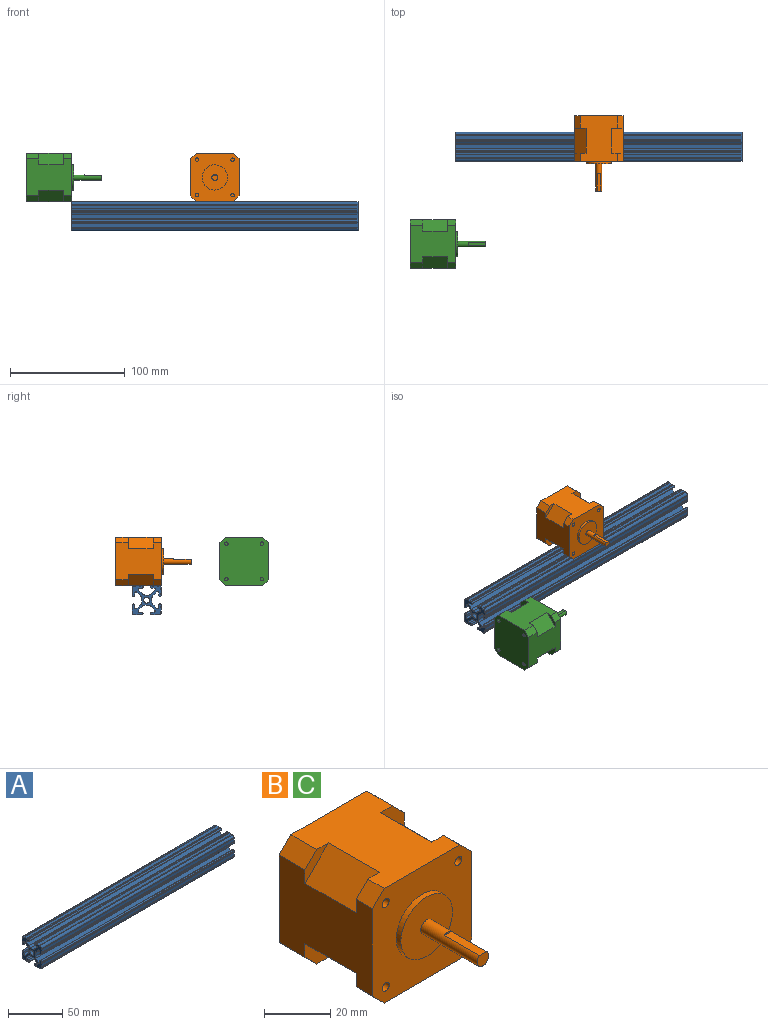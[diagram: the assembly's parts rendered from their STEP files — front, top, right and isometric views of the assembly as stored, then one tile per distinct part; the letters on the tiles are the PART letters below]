
ASSEMBLY  parts=3 mates=4
PART A: 99 faces, bbox 250x25.4x25.4 mm
  f0: cylinder r=2.6mm len=250mm, axis (-1,0,0), area 4089.6mm2, adj f1,f2
  f1: plane 25.4x25.4mm, normal (1,0,0), area 280.1mm2, adj f0,f3,f4,f5,f6,f7,f8,f9
  f2: plane 25.4x25.4mm, normal (-1,0,0), area 280.1mm2, adj f0,f3,f4,f5,f6,f7,f8,f9
  f3: plane 250x3.23mm, normal (0,0.71,0.71), area 1140mm2, adj f1,f2,f4,f98
  f4: cylinder r=1.08mm len=250mm, axis (-1,0,0), area 636.7mm2, adj f1,f2,f3,f5
  f5: plane 250x2.13mm, normal (0,-1,0), area 532.2mm2, adj f1,f2,f4,f6
  f6: cylinder r=1.06mm len=250mm, axis (-1,0,0), area 410.9mm2, adj f1,f2,f5,f7
  f7: plane 250x0.11mm, normal (0,0,1), area 27.9mm2, adj f1,f2,f6,f8
  f8: cylinder r=1.06mm len=250mm, axis (-1,0,0), area 410.9mm2, adj f1,f2,f7,f9
  f9: plane 250x1.03mm, normal (0,1,0), area 257.4mm2, adj f1,f2,f8,f10
  f10: cylinder r=0.51mm len=250mm, axis (-1,0,0), area 399mm2, adj f1,f2,f9,f11
  f11: plane 250x3.22mm, normal (0,1,0), area 804.3mm2, adj f1,f2,f10,f12
  f12: cylinder r=0.51mm len=250mm, axis (-1,0,0), area 398.9mm2, adj f1,f2,f11,f13
  f13: cylinder r=2.11mm len=250mm, axis (-1,0,0), area 840.6mm2, adj f1,f2,f12,f14
  f14: cylinder r=0.51mm len=250mm, axis (-1,0,0), area 398.9mm2, adj f1,f2,f13,f15
  f15: plane 250x3.22mm, normal (0,0,-1), area 804.4mm2, adj f1,f2,f14,f16
  f16: cylinder r=0.51mm len=250mm, axis (-1,0,0), area 399mm2, adj f1,f2,f15,f17
  f17: plane 250x1.03mm, normal (0,0,-1), area 257.4mm2, adj f1,f2,f16,f18
  f18: cylinder r=1.06mm len=250mm, axis (-1,0,0), area 410.9mm2, adj f1,f2,f17,f19
  f19: plane 250x0.11mm, normal (0,-1,0), area 27.9mm2, adj f1,f2,f18,f20
  f20: cylinder r=1.06mm len=250mm, axis (-1,0,0), area 410.9mm2, adj f1,f2,f19,f21
  f21: plane 250x2.11mm, normal (0,0,1), area 528.6mm2, adj f1,f2,f20,f22
  f22: cylinder r=1.03mm len=250mm, axis (-1,0,0), area 604.9mm2, adj f1,f2,f21,f23
  f23: plane 250x3.3mm, normal (0,-0.71,-0.71), area 1164mm2, adj f1,f2,f22,f24
  f24: cylinder r=3.19mm len=250mm, axis (-1,0,0), area 624.1mm2, adj f1,f2,f23,f25
  f25: plane 250x3.19mm, normal (0,0,-1), area 796.6mm2, adj f1,f2,f24,f26
  f26: cylinder r=3.2mm len=250mm, axis (-1,0,0), area 624.1mm2, adj f1,f2,f25,f27
  f27: plane 250x3.3mm, normal (0,0.71,-0.71), area 1164mm2, adj f1,f2,f26,f28
  f28: cylinder r=1.03mm len=250mm, axis (-1,0,0), area 604.9mm2, adj f1,f2,f27,f29
  f29: plane 250x2.11mm, normal (0,0,1), area 528.6mm2, adj f1,f2,f28,f30
  f30: cylinder r=1.06mm len=250mm, axis (-1,0,0), area 410.9mm2, adj f1,f2,f29,f31
  f31: plane 250x0.11mm, normal (0,1,0), area 27.9mm2, adj f1,f2,f30,f32
  f32: cylinder r=1.06mm len=250mm, axis (-1,0,0), area 410.9mm2, adj f1,f2,f31,f33
  f33: plane 250x1.03mm, normal (0,0,-1), area 257.4mm2, adj f1,f2,f32,f34
  f34: cylinder r=0.51mm len=250mm, axis (-1,0,0), area 399mm2, adj f1,f2,f33,f35
  f35: plane 250x3.22mm, normal (0,0,-1), area 804.3mm2, adj f1,f2,f34,f36
  f36: cylinder r=0.51mm len=250mm, axis (-1,0,0), area 398.9mm2, adj f1,f2,f35,f37
  f37: cylinder r=2.11mm len=250mm, axis (-1,0,0), area 840.6mm2, adj f1,f2,f36,f38
  f38: cylinder r=0.51mm len=250mm, axis (-1,0,0), area 399mm2, adj f1,f2,f37,f39
  f39: plane 250x3.22mm, normal (0,-1,0), area 804.3mm2, adj f1,f2,f38,f40
  f40: cylinder r=0.51mm len=250mm, axis (-1,0,0), area 399mm2, adj f1,f2,f39,f41
  f41: plane 250x1.03mm, normal (0,-1,0), area 257.4mm2, adj f1,f2,f40,f42
  f42: cylinder r=1.06mm len=250mm, axis (-1,0,0), area 410.9mm2, adj f1,f2,f41,f43
  f43: plane 250x0.11mm, normal (0,0,1), area 27.9mm2, adj f1,f2,f42,f44
  f44: cylinder r=1.06mm len=250mm, axis (-1,0,0), area 410.9mm2, adj f1,f2,f43,f45
  f45: plane 250x2.19mm, normal (0,1,0), area 547.3mm2, adj f1,f2,f44,f46
  f46: cylinder r=1.03mm len=250mm, axis (-1,0,0), area 609.4mm2, adj f1,f2,f45,f47
  f47: plane 250x3.31mm, normal (0,-0.71,0.71), area 1168.5mm2, adj f1,f2,f46,f48
  f48: cylinder r=3.2mm len=250mm, axis (-1,0,0), area 622.2mm2, adj f1,f2,f47,f49
  f49: plane 250x3.31mm, normal (0,-1,0), area 827.9mm2, adj f1,f2,f48,f50
  f50: cylinder r=3.2mm len=250mm, axis (-1,0,0), area 622.3mm2, adj f1,f2,f49,f51
  f51: plane 250x3.31mm, normal (0,-0.71,-0.71), area 1168.5mm2, adj f1,f2,f50,f52
  f52: cylinder r=1.03mm len=250mm, axis (-1,0,0), area 609.4mm2, adj f1,f2,f51,f53
  f53: plane 250x2.19mm, normal (0,1,0), area 547.3mm2, adj f1,f2,f52,f54
  f54: cylinder r=1.06mm len=250mm, axis (-1,0,0), area 410.9mm2, adj f1,f2,f53,f55
  f55: plane 250x0.11mm, normal (0,0,-1), area 27.9mm2, adj f1,f2,f54,f56
  f56: cylinder r=1.06mm len=250mm, axis (-1,0,0), area 410.9mm2, adj f1,f2,f55,f57
  f57: plane 250x1.03mm, normal (0,-1,0), area 257.4mm2, adj f1,f2,f56,f58
  f58: cylinder r=0.51mm len=250mm, axis (-1,0,0), area 399mm2, adj f1,f2,f57,f59
  f59: plane 250x3.22mm, normal (0,-1,0), area 804.3mm2, adj f1,f2,f58,f60
  f60: cylinder r=0.51mm len=250mm, axis (-1,0,0), area 399mm2, adj f1,f2,f59,f61
  f61: cylinder r=2.11mm len=250mm, axis (-1,0,0), area 840.6mm2, adj f1,f2,f60,f62
  f62: cylinder r=0.51mm len=250mm, axis (-1,0,0), area 398.9mm2, adj f1,f2,f61,f63
  f63: plane 250x3.22mm, normal (0,0,1), area 804.3mm2, adj f1,f2,f62,f64
  f64: cylinder r=0.51mm len=250mm, axis (-1,0,0), area 399mm2, adj f1,f2,f63,f65
  f65: plane 250x1.03mm, normal (0,0,1), area 257.4mm2, adj f1,f2,f64,f66
  f66: cylinder r=1.06mm len=250mm, axis (-1,0,0), area 410.9mm2, adj f1,f2,f65,f67
  f67: plane 250x0.11mm, normal (0,1,0), area 27.9mm2, adj f1,f2,f66,f68
  f68: cylinder r=1.06mm len=250mm, axis (-1,0,0), area 410.9mm2, adj f1,f2,f67,f69
  f69: plane 250x2.11mm, normal (0,0,-1), area 528.6mm2, adj f1,f2,f68,f70
  f70: cylinder r=1.03mm len=250mm, axis (-1,0,0), area 604.9mm2, adj f1,f2,f69,f71
  f71: plane 250x3.3mm, normal (0,0.71,0.71), area 1164.1mm2, adj f1,f2,f70,f72
  f72: cylinder r=3.19mm len=250mm, axis (-1,0,0), area 624mm2, adj f1,f2,f71,f73
  f73: plane 250x3.19mm, normal (0,0,1), area 796.6mm2, adj f1,f2,f72,f74
  f74: cylinder r=3.19mm len=250mm, axis (-1,0,0), area 624.1mm2, adj f1,f2,f73,f75
  f75: plane 250x3.3mm, normal (0,-0.71,0.71), area 1164mm2, adj f1,f2,f74,f76
  f76: cylinder r=1.03mm len=250mm, axis (-1,0,0), area 604.9mm2, adj f1,f2,f75,f77
  f77: plane 250x2.11mm, normal (0,0,-1), area 528.6mm2, adj f1,f2,f76,f78
  f78: cylinder r=1.06mm len=250mm, axis (-1,0,0), area 410.9mm2, adj f1,f2,f77,f79
  f79: plane 250x0.11mm, normal (0,-1,0), area 27.9mm2, adj f1,f2,f78,f80
  f80: cylinder r=1.06mm len=250mm, axis (-1,0,0), area 410.9mm2, adj f1,f2,f79,f81
  f81: plane 250x1.03mm, normal (0,0,1), area 257.4mm2, adj f1,f2,f80,f82
  f82: cylinder r=0.51mm len=250mm, axis (-1,0,0), area 399mm2, adj f1,f2,f81,f83
  f83: plane 250x3.22mm, normal (0,0,1), area 804.4mm2, adj f1,f2,f82,f84
  f84: cylinder r=0.51mm len=250mm, axis (-1,0,0), area 398.9mm2, adj f1,f2,f83,f85
  f85: cylinder r=2.11mm len=250mm, axis (-1,0,0), area 840.6mm2, adj f1,f2,f84,f86
  f86: cylinder r=0.51mm len=250mm, axis (-1,0,0), area 398.9mm2, adj f1,f2,f85,f87
  f87: plane 250x3.22mm, normal (0,1,0), area 804.3mm2, adj f1,f2,f86,f88
  f88: cylinder r=0.51mm len=250mm, axis (-1,0,0), area 399mm2, adj f1,f2,f87,f89
  f89: plane 250x1.03mm, normal (0,1,0), area 257.4mm2, adj f1,f2,f88,f90
  f90: cylinder r=1.06mm len=250mm, axis (-1,0,0), area 410.9mm2, adj f1,f2,f89,f91
  f91: plane 250x0.11mm, normal (0,0,-1), area 27.9mm2, adj f1,f2,f90,f92
  f92: cylinder r=1.06mm len=250mm, axis (-1,0,0), area 410.9mm2, adj f1,f2,f91,f93
  f93: plane 250x2.13mm, normal (0,-1,0), area 532.3mm2, adj f1,f2,f92,f94
  f94: cylinder r=1.08mm len=250mm, axis (-1,0,0), area 636.6mm2, adj f1,f2,f93,f95
  f95: plane 250x3.23mm, normal (0,0.71,-0.71), area 1140mm2, adj f1,f2,f94,f96
  f96: cylinder r=3.19mm len=250mm, axis (-1,0,0), area 622.5mm2, adj f1,f2,f95,f97
  f97: plane 250x3.42mm, normal (0,1,0), area 854.6mm2, adj f1,f2,f96,f98
  f98: cylinder r=3.19mm len=250mm, axis (-1,0,0), area 622.5mm2, adj f1,f2,f3,f97
PART B: 48 faces, bbox 42.3x65.8x42.3 mm
  f0: plane 10x10mm, normal (0,1,0), area 37.5mm2, adj f4,f5,f9,f27
  f1: plane 10x10mm, normal (0,1,0), area 37.5mm2, adj f5,f6,f10,f30
  f2: plane 10x10mm, normal (0,1,0), area 37.5mm2, adj f6,f7,f11,f29
  f3: plane 42.3x42.3mm, normal (0,-1,0), area 1330.9mm2, adj f4,f5,f6,f7,f9,f10,f11,f12
  f4: plane 39.8x32.3mm, normal (-1,0,0), area 1067.5mm2, adj f0,f3,f8,f9,f12,f27,f28,f31
  f5: plane 39.8x32.3mm, normal (0,0,-1), area 1067.5mm2, adj f0,f1,f3,f9,f10,f27,f30,f31
  f6: plane 39.8x32.3mm, normal (1,0,0), area 1067.5mm2, adj f1,f2,f3,f10,f11,f29,f30,f33
  f7: plane 39.8x32.3mm, normal (0,0,1), area 1067.5mm2, adj f2,f3,f8,f11,f12,f28,f29,f32
  f8: plane 10x10mm, normal (0,1,0), area 37.5mm2, adj f4,f7,f12,f28
  f9: plane 7x5mm, normal (-0.71,0,-0.71), area 49.5mm2, adj f0,f3,f4,f5
  f10: plane 7x5mm, normal (0.71,0,-0.71), area 49.5mm2, adj f1,f3,f5,f6
  f11: plane 7x5mm, normal (0.71,0,0.71), area 49.5mm2, adj f2,f3,f6,f7
  f12: plane 7x5mm, normal (-0.71,0,0.71), area 49.5mm2, adj f3,f4,f7,f8
  f13: cylinder r=11mm len=22mm, axis (0,1,0), area 138.2mm2, adj f3,f14
  f14: plane 22x22mm, normal (0,-1,0), area 360.5mm2, adj f13,f23
  f15: cylinder r=1.5mm len=4.5mm, axis (0,-1,0), area 42.4mm2, adj f3,f16
  f16: plane 3x3mm, normal (0,-1,0), area 7.1mm2, adj f15
  f17: cylinder r=1.5mm len=4.5mm, axis (0,-1,0), area 42.4mm2, adj f3,f18
  f18: plane 3x3mm, normal (0,-1,0), area 7.1mm2, adj f17
  f19: cylinder r=1.5mm len=4.5mm, axis (0,-1,0), area 42.4mm2, adj f3,f20
  f20: plane 3x3mm, normal (0,-1,0), area 7.1mm2, adj f19
  f21: cylinder r=1.5mm len=4.5mm, axis (0,-1,0), area 42.4mm2, adj f3,f22
  f22: plane 3x3mm, normal (0,-1,0), area 7.1mm2, adj f21
  f23: cylinder r=2.5mm len=24mm, axis (0,1,0), area 328.7mm2, adj f14,f24,f25,f26
  f24: plane 5x4.5mm, normal (0,-1,0), area 18.6mm2, adj f23,f25
  f25: plane 15x3mm, normal (0,0,1), area 45mm2, adj f23,f24,f26
  f26: plane 3x0.5mm, normal (0,-1,0), area 1mm2, adj f23,f25
  f27: plane 21.8x10mm, normal (-0.71,0,-0.71), area 308.3mm2, adj f0,f4,f5,f31
  f28: plane 21.8x10mm, normal (-0.71,0,0.71), area 308.3mm2, adj f4,f7,f8,f32
  f29: plane 21.8x10mm, normal (0.71,0,0.71), area 308.3mm2, adj f2,f6,f7,f33
  f30: plane 21.8x10mm, normal (0.71,0,-0.71), area 308.3mm2, adj f1,f5,f6,f34
  f31: plane 10x10mm, normal (0,-1,0), area 37.5mm2, adj f4,f5,f27,f37
  f32: plane 10x10mm, normal (0,-1,0), area 37.5mm2, adj f4,f7,f28,f36
  f33: plane 10x10mm, normal (0,-1,0), area 37.5mm2, adj f6,f7,f29,f39
  f34: plane 10x10mm, normal (0,-1,0), area 37.5mm2, adj f5,f6,f30,f38
  f35: plane 42.3x42.3mm, normal (0,1,0), area 1711mm2, adj f4,f5,f6,f7,f36,f37,f38,f39
  f36: plane 11x5mm, normal (-0.71,0,0.71), area 77.8mm2, adj f4,f7,f32,f35
  f37: plane 11x5mm, normal (-0.71,0,-0.71), area 77.8mm2, adj f4,f5,f31,f35
  f38: plane 11x5mm, normal (0.71,0,-0.71), area 77.8mm2, adj f5,f6,f34,f35
  f39: plane 11x5mm, normal (0.71,0,0.71), area 77.8mm2, adj f6,f7,f33,f35
  f40: cylinder r=1.5mm len=4.5mm, axis (0,1,0), area 42.4mm2, adj f35,f41
  f41: plane 3x3mm, normal (0,1,0), area 7.1mm2, adj f40
  f42: cylinder r=1.5mm len=4.5mm, axis (0,1,0), area 42.4mm2, adj f35,f43
  f43: plane 3x3mm, normal (0,1,0), area 7.1mm2, adj f42
  f44: cylinder r=1.5mm len=4.5mm, axis (0,1,0), area 42.4mm2, adj f35,f45
  f45: plane 3x3mm, normal (0,1,0), area 7.1mm2, adj f44
  f46: cylinder r=1.5mm len=4.5mm, axis (0,1,0), area 42.4mm2, adj f35,f47
  f47: plane 3x3mm, normal (0,1,0), area 7.1mm2, adj f46
PART C: same geometry as B
PLACE A at identity fixed
PLACE B t=(18.45,69.3,33.12)mm
PLACE C rot(axis=(0,0,1),90deg) t=(-132,8.45,33.12)mm
MATE planar A.f0 <-> C.f13  axis (-1,0,0) through (-125,75,12.7)mm
MATE planar B.f5 <-> A.f63  axis (0,0,-1) through (0,82.61,25.4)mm
MATE planar A.f63 <-> C.f5  axis (0,0,1) through (0,67.06,25.4)mm
MATE planar B.f13 <-> A.f59  axis (0,-1,0) through (0,62.3,46.55)mm
